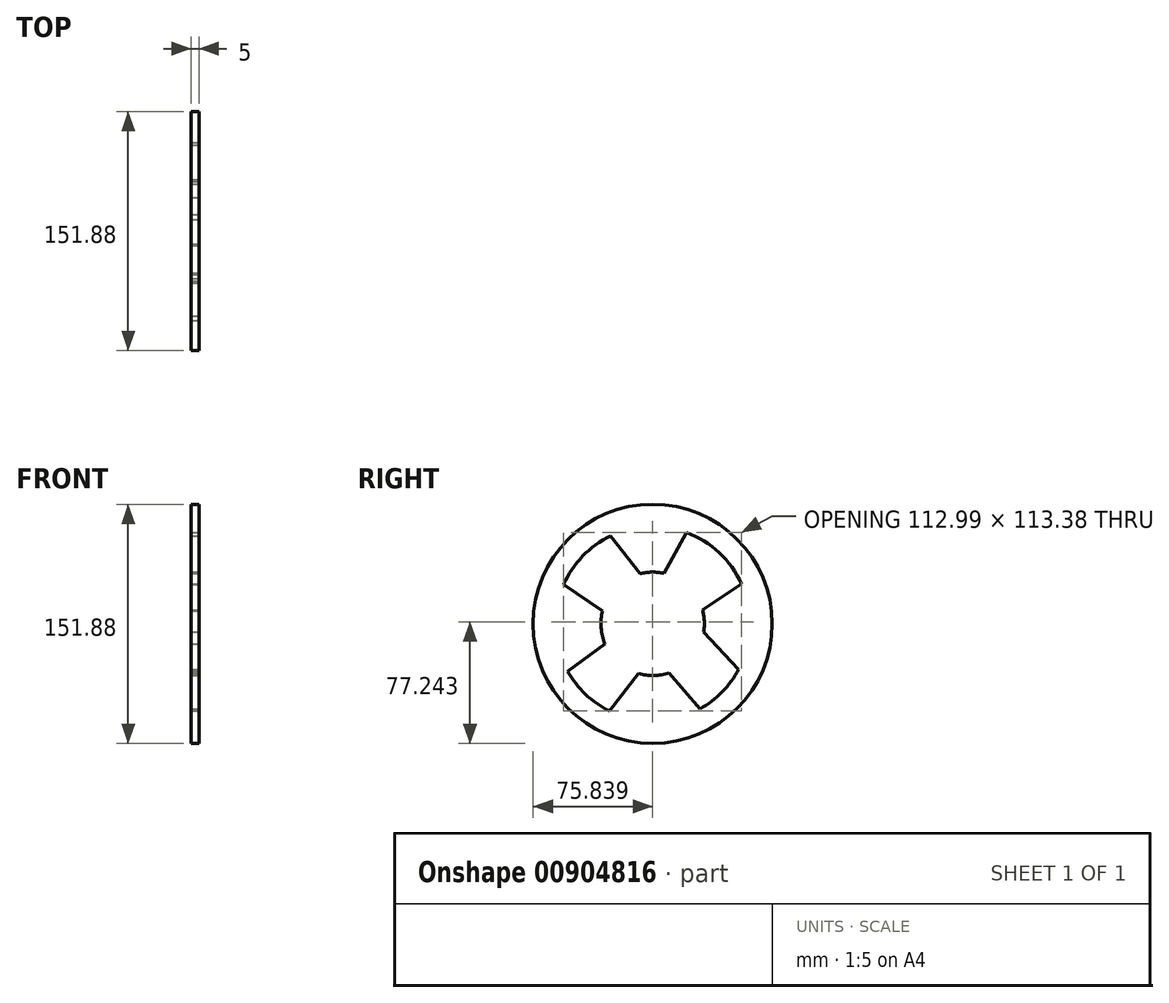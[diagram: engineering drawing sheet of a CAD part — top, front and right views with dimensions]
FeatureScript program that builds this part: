
annotation { "Feature Type Name" : "Feature", "Feature Type Description" : "" }
export const myFeature = defineFeature(function(context is Context, id is Id, definition is map)
    precondition{}
    {
        {
            var Q0;
            Q0=qCreatedBy(makeId("Right.planeOp"),FACE);
            var sketch = newSketch(context, id + "F0", { "sketchPlane" : qUnion([Q0])});
            skCircle(sketch, "E0", {"center": v(0, 0) * mm, "radius": 68.52 * mm});
            skCircle(sketch, "E1", {"center": v(0, 0) * mm, "radius": 61.82 * mm});
            skCircle(sketch, "E2", {"center": v(0, 0) * mm, "radius": 75.94 * mm});
            skCircle(sketch, "E3", {"center": v(0, 0) * mm, "radius": 32.84 * mm});
            skLineSegment(sketch, "E4", {"start": v(-26.73, 55.74) * mm, "end": v(-8.05, 31.84) * mm});
            skLineSegment(sketch, "E5", {"start": v(21.41, 58) * mm, "end": v(7.32, 32.01) * mm});
            skLineSegment(sketch, "E6", {"start": v(31.6, 8.93) * mm, "end": v(56.4, 25.32) * mm});
            skLineSegment(sketch, "E7", {"start": v(32.43, -5.16) * mm, "end": v(54.66, -28.87) * mm});
            skLineSegment(sketch, "E8", {"start": v(10.48, -31.12) * mm, "end": v(29.95, -54.08) * mm});
            skLineSegment(sketch, "E9", {"start": v(-9, -31.59) * mm, "end": v(-27.46, -55.38) * mm});
            skLineSegment(sketch, "E10", {"start": v(-30.24, -12.82) * mm, "end": v(-53.97, -30.14) * mm});
            skLineSegment(sketch, "E11", {"start": v(-31.8, 8.23) * mm, "end": v(-56.6, 24.86) * mm});
            skSolve(sketch);
        }
        {
            var Q0;
            Q0=makeQuery(id+"F0.imprint","IMPRINT",FACE,{"disambiguationData":[TD([[makeQuery(id+"F0.imprint","IMPRINT",EDGE,{"derivedFrom":sQuery(id+"F0.wireOp",EDGE,"E0")}),-1.0]])]});
            var Q1;
            Q1=makeQuery(id+"F0.imprint","IMPRINT",FACE,{"disambiguationData":[TD([[makeQuery(id+"F0.imprint","IMPRINT",EDGE,{"derivedFrom":sQuery(id+"F0.wireOp",EDGE,"E0")}),1.0]])]});
            var Q2;
            {var subQ0=sQuery(id+"F0.wireOp",EDGE,"E10");Q2=makeQuery(id+"F0.imprint","IMPRINT",FACE,{"disambiguationData":[TD([[makeQuery(id+"F0.imprint","IMPRINT",EDGE,{"derivedFrom":subQ0}),-1.0]])]});}
            var Q3;
            {var subQ0=sQuery(id+"F0.wireOp",EDGE,"E4");Q3=makeQuery(id+"F0.imprint","IMPRINT",FACE,{"disambiguationData":[TD([[makeQuery(id+"F0.imprint","IMPRINT",EDGE,{"derivedFrom":subQ0}),1.0]])]});}
            var Q4;
            {var subQ0=sQuery(id+"F0.wireOp",EDGE,"E8");Q4=makeQuery(id+"F0.imprint","IMPRINT",FACE,{"disambiguationData":[TD([[makeQuery(id+"F0.imprint","IMPRINT",EDGE,{"derivedFrom":subQ0}),-1.0]])]});}
            var Q5;
            {var subQ0=sQuery(id+"F0.wireOp",EDGE,"E6");Q5=makeQuery(id+"F0.imprint","IMPRINT",FACE,{"disambiguationData":[TD([[makeQuery(id+"F0.imprint","IMPRINT",EDGE,{"derivedFrom":subQ0}),-1.0]])]});}
            extrude(context, id + "F1", {"entities" : qUnion([Q0, Q1, Q2, Q3, Q4, Q5]), "oppositeDirection" : true, "depth" : 5 * mm, "offsetDistance" : 25.4 * mm});
        }
    });
